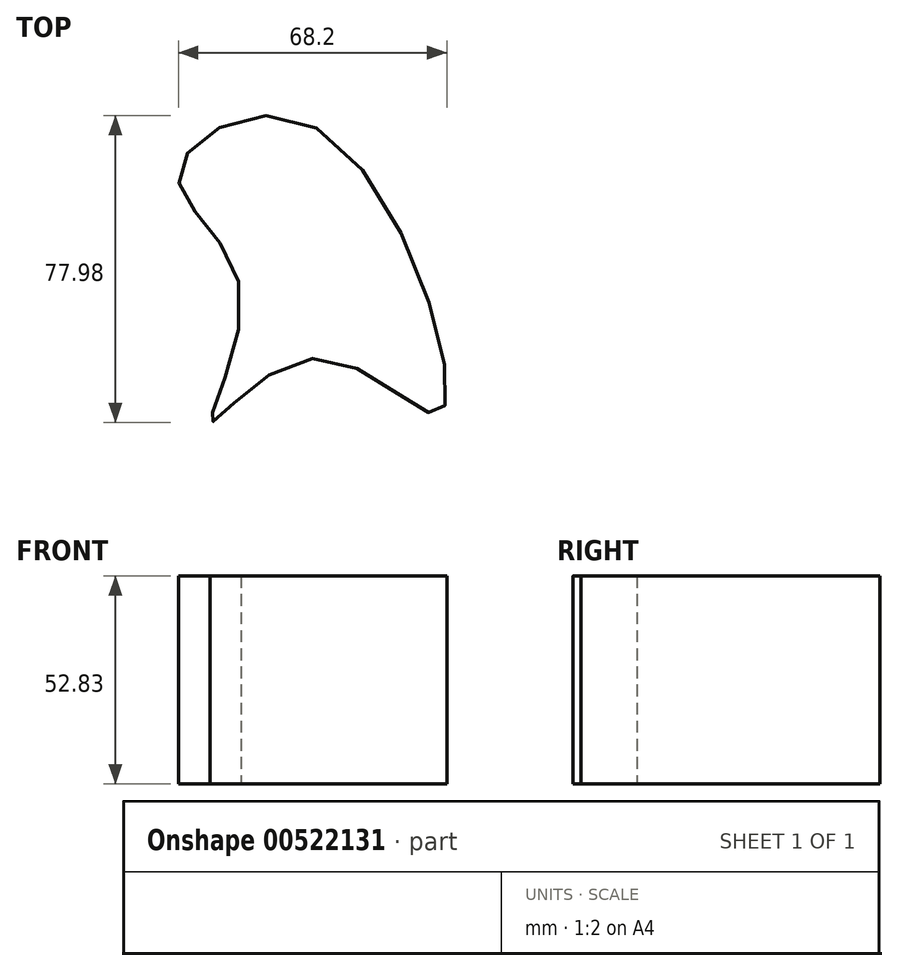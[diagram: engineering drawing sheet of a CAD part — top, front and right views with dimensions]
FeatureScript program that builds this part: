
annotation { "Feature Type Name" : "Feature", "Feature Type Description" : "" }
export const myFeature = defineFeature(function(context is Context, id is Id, definition is map)
    precondition{}
    {
        {
            var Q0;
            Q0=qCreatedBy(makeId("Top.planeOp"),FACE);
            var sketch = newSketch(context, id + "F0", { "sketchPlane" : qUnion([Q0])});
            skFitSpline(sketch, "E0", {"points": [v(0, 40.57) * mm, v(-35.01, 29.09) * mm, v(-19.45, 0) * mm, v(-26.86, -34.27) * mm, v(0, -17.97) * mm, v(31.68, -31.68) * mm, v(0, 40.57) * mm]});
            skSolve(sketch);
        }
        {
            var Q0;
            Q0=makeQuery(id+"F0.imprint","IMPRINT",FACE,{"disambiguationData":[TD([[makeQuery(id+"F0.imprint","IMPRINT",EDGE,{"derivedFrom":sQuery(id+"F0.wireOp",EDGE,"E0")}),1.0]])]});
            extrude(context, id + "F1", {"entities" : qUnion([Q0]), "depth" : 52.83 * mm, "offsetDistance" : 25.4 * mm});
        }
    });
